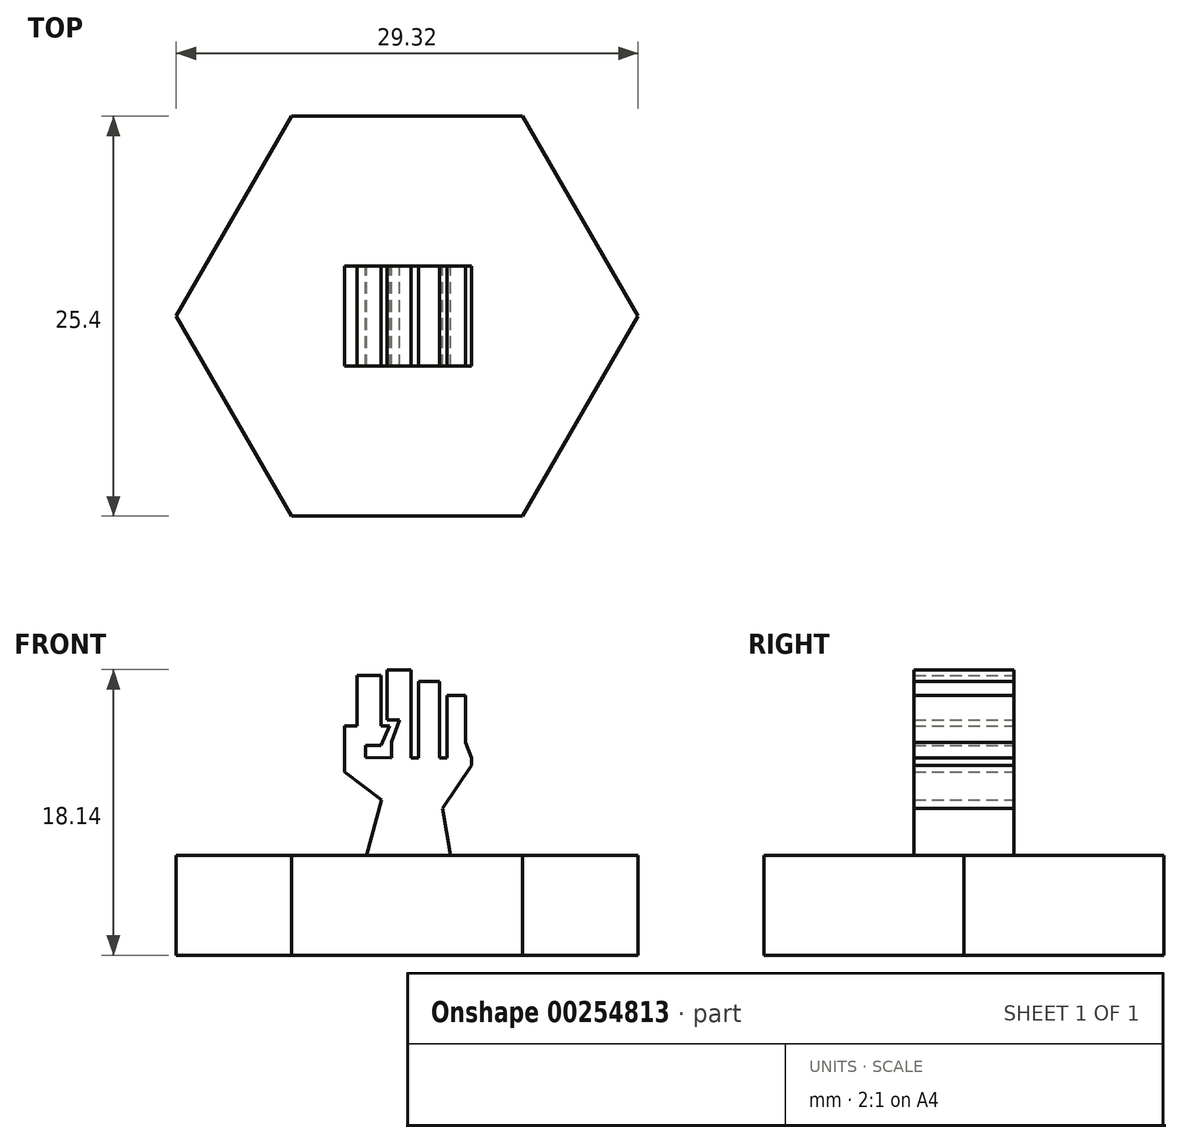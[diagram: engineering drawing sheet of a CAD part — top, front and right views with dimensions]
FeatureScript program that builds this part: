
annotation { "Feature Type Name" : "Feature", "Feature Type Description" : "" }
export const myFeature = defineFeature(function(context is Context, id is Id, definition is map)
    precondition{}
    {
        {
            var Q0;
            Q0=qCreatedBy(makeId("Top.planeOp"),FACE);
            var sketch = newSketch(context, id + "F0", { "sketchPlane" : qUnion([Q0])});
            skCircle(sketch, "E0.cCircle", {"center": v(0, 0) * mm, "radius": 12.7 * mm, "construction": true});
            skLineSegment(sketch, "E0.0", {"start": v(-7.33, 12.7) * mm, "end": v(7.33, 12.7) * mm});
            skLineSegment(sketch, "E0.1", {"start": v(7.33, 12.7) * mm, "end": v(14.66, 0) * mm});
            skLineSegment(sketch, "E0.2", {"start": v(14.66, 0) * mm, "end": v(7.33, -12.7) * mm});
            skLineSegment(sketch, "E0.3", {"start": v(7.33, -12.7) * mm, "end": v(-7.33, -12.7) * mm});
            skLineSegment(sketch, "E0.4", {"start": v(-7.33, -12.7) * mm, "end": v(-14.66, 0) * mm});
            skLineSegment(sketch, "E0.5", {"start": v(-14.66, 0) * mm, "end": v(-7.33, 12.7) * mm});
            skPoint(sketch, "E0.0.midPoint", {"position": v(0, 12.7) * mm});
            skSolve(sketch);
        }
        {
            var Q0;
            Q0 = qSketchRegion(id + "F0", true);
            extrude(context, id + "F1", {"entities" : qUnion([Q0]), "depth" : 6.35 * mm});
        }
        {
            var Q0;
            Q0=qCreatedBy(makeId("Front.planeOp"),FACE);
            var sketch = newSketch(context, id + "F2", { "sketchPlane" : qUnion([Q0])});
            skLineSegment(sketch, "E1", {"start": v(-2.58, 6.35) * mm, "end": v(-1.63, 9.88) * mm});
            skLineSegment(sketch, "E2", {"start": v(2.24, 9.32) * mm, "end": v(2.77, 6.35) * mm});
            skLineSegment(sketch, "E3", {"start": v(2.77, 6.35) * mm, "end": v(-2.58, 6.35) * mm});
            skLineSegment(sketch, "E4", {"start": v(-3.98, 11.63) * mm, "end": v(-1.63, 9.88) * mm});
            skLineSegment(sketch, "E5", {"start": v(-3.98, 11.63) * mm, "end": v(-3.98, 14.56) * mm});
            skLineSegment(sketch, "E6", {"start": v(-3.98, 14.56) * mm, "end": v(-1.12, 14.56) * mm});
            skLineSegment(sketch, "E7", {"start": v(-1.12, 14.56) * mm, "end": v(-1.64, 13.33) * mm});
            skLineSegment(sketch, "E8", {"start": v(-1.64, 13.33) * mm, "end": v(-2.65, 13.33) * mm});
            skLineSegment(sketch, "E9", {"start": v(-2.65, 13.33) * mm, "end": v(-2.65, 12.55) * mm});
            skLineSegment(sketch, "E10", {"start": v(-3.18, 17.77) * mm, "end": v(-3.18, 14.56) * mm});
            skLineSegment(sketch, "E11", {"start": v(-3.18, 17.77) * mm, "end": v(-1.67, 17.77) * mm});
            skLineSegment(sketch, "E12", {"start": v(-1.67, 17.77) * mm, "end": v(-1.67, 14.56) * mm});
            skLineSegment(sketch, "E13", {"start": v(0.24, 18.14) * mm, "end": v(-1.26, 18.14) * mm});
            skLineSegment(sketch, "E14", {"start": v(-1.26, 18.14) * mm, "end": v(-1.26, 14.96) * mm});
            skLineSegment(sketch, "E15", {"start": v(-1.26, 14.96) * mm, "end": v(-0.5, 14.96) * mm});
            skLineSegment(sketch, "E16", {"start": v(-0.5, 14.96) * mm, "end": v(-1, 13.56) * mm});
            skLineSegment(sketch, "E17", {"start": v(2.24, 9.32) * mm, "end": v(4.1, 12.07) * mm});
            skLineSegment(sketch, "E18", {"start": v(4.1, 12.07) * mm, "end": v(4.1, 12.53) * mm});
            skLineSegment(sketch, "E19", {"start": v(4.1, 12.53) * mm, "end": v(3.71, 13.52) * mm});
            skLineSegment(sketch, "E20", {"start": v(0.72, 17.4) * mm, "end": v(2.07, 17.4) * mm});
            skLineSegment(sketch, "E21", {"start": v(3.71, 13.52) * mm, "end": v(3.71, 16.5) * mm});
            skLineSegment(sketch, "E22", {"start": v(3.71, 16.5) * mm, "end": v(2.53, 16.5) * mm});
            skLineSegment(sketch, "E23", {"start": v(-2.65, 12.55) * mm, "end": v(4.1, 12.53) * mm});
            skLineSegment(sketch, "E24", {"start": v(2.53, 16.5) * mm, "end": v(2.53, 12.53) * mm});
            skLineSegment(sketch, "E25", {"start": v(-1, 13.56) * mm, "end": v(-1, 12.54) * mm});
            skLineSegment(sketch, "E26", {"start": v(0.24, 18.14) * mm, "end": v(0.24, 12.54) * mm});
            skLineSegment(sketch, "E27", {"start": v(0.72, 17.4) * mm, "end": v(0.72, 12.54) * mm});
            skLineSegment(sketch, "E28", {"start": v(2.07, 17.4) * mm, "end": v(2.07, 12.54) * mm});
            skSolve(sketch);
        }
        {
            var Q0;
            Q0 = qSketchRegion(id + "F2", true);
            extrude(context, id + "F3", {"entities" : qUnion([Q0]), "operationType" : NewBodyOperationType.ADD, "endBound" : BoundingType.SYMMETRIC, "depth" : 6.35 * mm});
        }
    });
